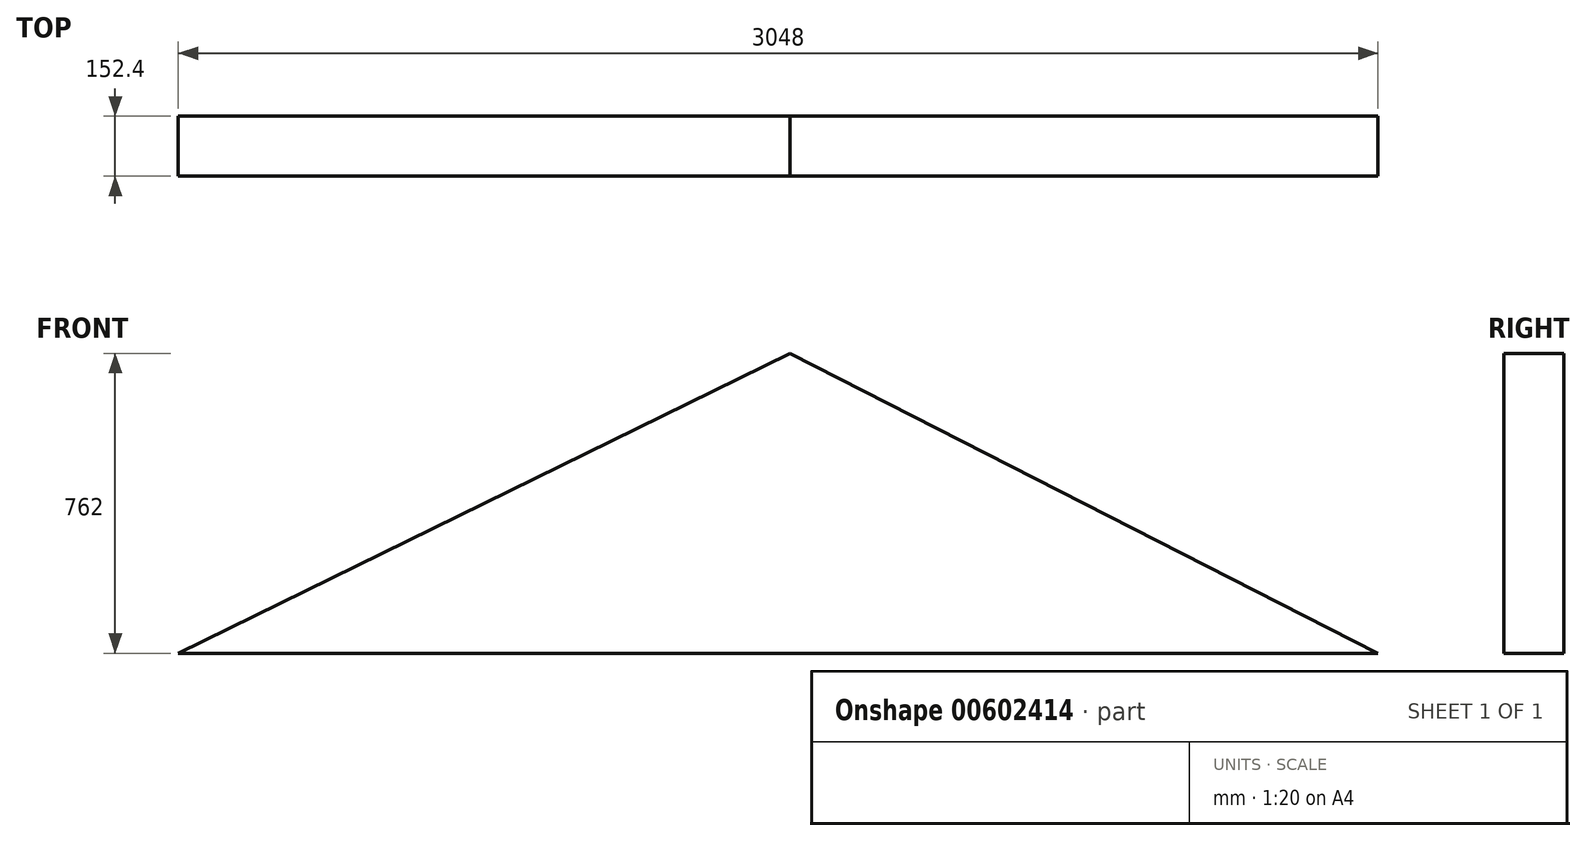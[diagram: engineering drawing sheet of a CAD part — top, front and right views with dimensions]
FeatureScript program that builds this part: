
annotation { "Feature Type Name" : "Feature", "Feature Type Description" : "" }
export const myFeature = defineFeature(function(context is Context, id is Id, definition is map)
    precondition{}
    {
        {
            var Q0;
            Q0=qCreatedBy(makeId("Front.planeOp"),FACE);
            var sketch = newSketch(context, id + "F0", { "sketchPlane" : qUnion([Q0])});
            skLineSegment(sketch, "E0", {"start": v(-1553.63, 0) * mm, "end": v(1494.37, 0) * mm});
            skLineSegment(sketch, "E1", {"start": v(1494.37, 0) * mm, "end": v(0, 762) * mm});
            skLineSegment(sketch, "E2", {"start": v(0, 762) * mm, "end": v(-1553.63, 0) * mm});
            skLineSegment(sketch, "E3", {"start": v(0, 762) * mm, "end": v(0, 0) * mm, "construction": true});
            skSolve(sketch);
        }
        {
            var Q0;
            Q0=makeQuery(id+"F0.imprint","IMPRINT",FACE,{"disambiguationData":[TD([[makeQuery(id+"F0.imprint","IMPRINT",EDGE,{"derivedFrom":sQuery(id+"F0.wireOp",EDGE,"E0")}),1.0]])]});
            extrude(context, id + "F1", {"entities" : qUnion([Q0]), "depth" : 152.4 * mm, "offsetDistance" : 30.48 * mm});
        }
    });
